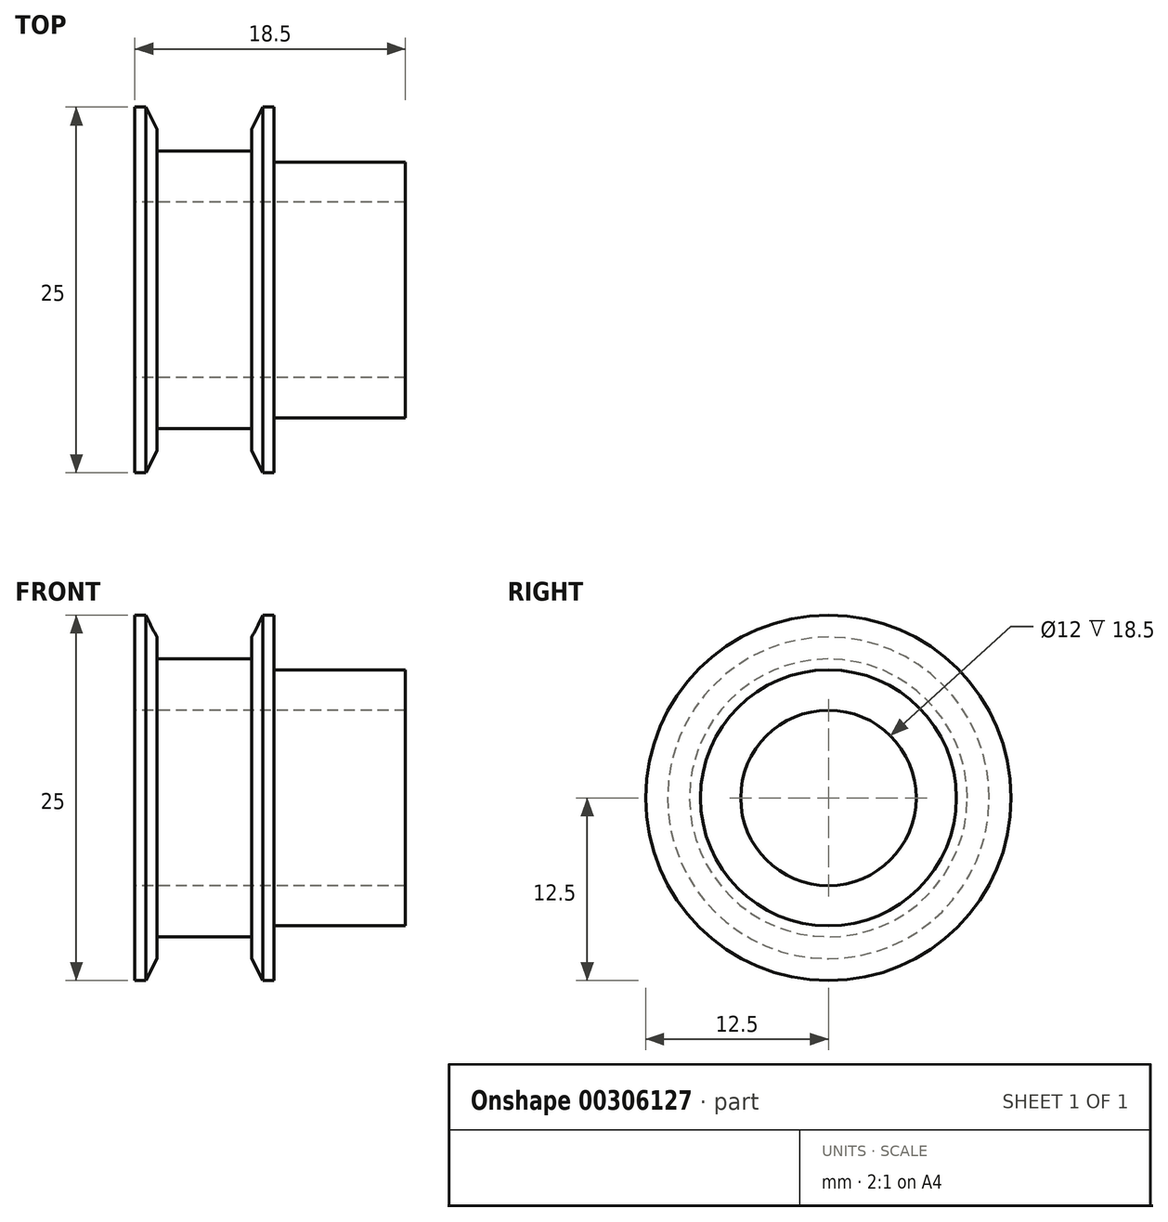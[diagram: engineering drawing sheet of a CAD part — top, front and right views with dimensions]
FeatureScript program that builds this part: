
annotation { "Feature Type Name" : "Feature", "Feature Type Description" : "" }
export const myFeature = defineFeature(function(context is Context, id is Id, definition is map)
    precondition{}
    {
        {
            var Q0;
            Q0=qCreatedBy(makeId("Front.planeOp"),FACE);
            var sketch = newSketch(context, id + "F0", { "sketchPlane" : qUnion([Q0])});
            skPoint(sketch, "E0", {"position": v(0, 6) * mm});
            skLineSegment(sketch, "E1", {"start": v(0, 6) * mm, "end": v(0, 12.5) * mm});
            skLineSegment(sketch, "E2", {"start": v(1.5, 11) * mm, "end": v(1.5, 9.5) * mm});
            skLineSegment(sketch, "E3", {"start": v(1.5, 9.5) * mm, "end": v(8, 9.5) * mm});
            skLineSegment(sketch, "E4", {"start": v(9.5, 12.5) * mm, "end": v(9.5, 8.75) * mm});
            skLineSegment(sketch, "E5", {"start": v(0, 0) * mm, "end": v(21.58, 0) * mm});
            skLineSegment(sketch, "E6", {"start": v(18.5, 8.75) * mm, "end": v(9.5, 8.75) * mm});
            skLineSegment(sketch, "E7", {"start": v(0.75, 12.5) * mm, "end": v(1.5, 11) * mm});
            skLineSegment(sketch, "E8", {"start": v(8.75, 12.5) * mm, "end": v(8, 11) * mm});
            skLineSegment(sketch, "E9", {"start": v(0, 12.5) * mm, "end": v(0.75, 12.5) * mm});
            skLineSegment(sketch, "E10", {"start": v(8.75, 12.5) * mm, "end": v(9.5, 12.5) * mm});
            skLineSegment(sketch, "E11", {"start": v(8, 11) * mm, "end": v(8, 9.5) * mm});
            skPoint(sketch, "E12", {"position": v(18.5, 8.75) * mm});
            skLineSegment(sketch, "E13", {"start": v(18.5, 8.75) * mm, "end": v(18.5, 6) * mm});
            skLineSegment(sketch, "E14", {"start": v(18.5, 6) * mm, "end": v(0, 6) * mm});
            skSolve(sketch);
        }
        {
            var Q0;
            Q0=makeQuery(id+"F0.imprint","IMPRINT",FACE,{"disambiguationData":[TD([[makeQuery(id+"F0.imprint","IMPRINT",EDGE,{"derivedFrom":sQuery(id+"F0.wireOp",EDGE,"E1")}),-1.0]])]});
            var Q1;
            Q1=sQuery(id+"F0.wireOp",EDGE,"E5");
            revolve(context, id + "F1", {"entities" : qUnion([Q0]), "axis" : qUnion([Q1]), "revolveType" : RevolveType.FULL});
        }
    });
